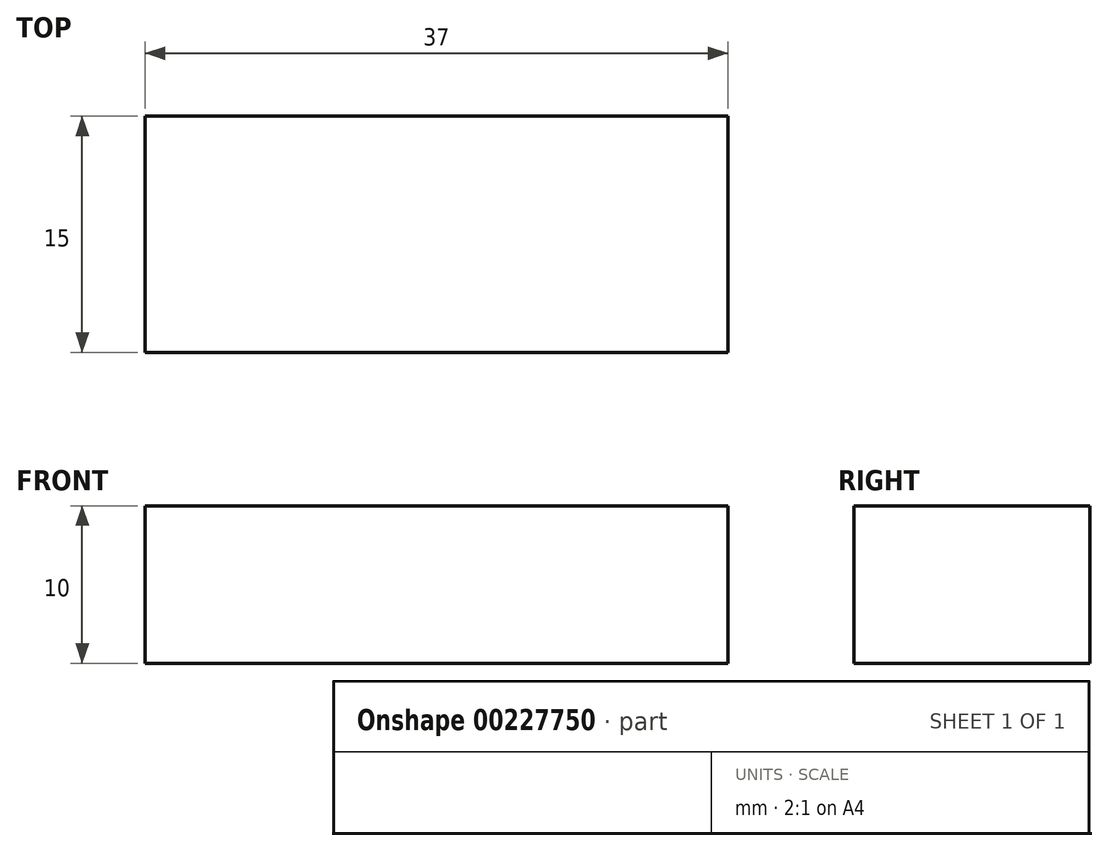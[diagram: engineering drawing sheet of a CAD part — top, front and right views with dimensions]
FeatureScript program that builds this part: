
annotation { "Feature Type Name" : "Feature", "Feature Type Description" : "" }
export const myFeature = defineFeature(function(context is Context, id is Id, definition is map)
    precondition{}
    {
        {
            var Q0;
            Q0=qCreatedBy(makeId("Top.planeOp"),FACE);
            var sketch = newSketch(context, id + "F0", { "sketchPlane" : qUnion([Q0])});
            skLineSegment(sketch, "E0.bottom", {"start": v(-18.5, 7.5) * mm, "end": v(18.5, 7.5) * mm});
            skLineSegment(sketch, "E0.top", {"start": v(-18.5, -7.5) * mm, "end": v(18.5, -7.5) * mm});
            skLineSegment(sketch, "E0.left", {"start": v(-18.5, 7.5) * mm, "end": v(-18.5, -7.5) * mm});
            skLineSegment(sketch, "E0.right", {"start": v(18.5, 7.5) * mm, "end": v(18.5, -7.5) * mm});
            skPoint(sketch, "E1", {"position": v(0, 0) * mm});
            skPoint(sketch, "E1.positionSnap0", {"position": v(18.5, 0) * mm});
            skPoint(sketch, "E1.positionSnap1", {"position": v(0, -7.5) * mm});
            skSolve(sketch);
        }
        {
            var Q0;
            Q0=makeQuery(id+"F0.imprint","IMPRINT",FACE,{"disambiguationData":[TD([[makeQuery(id+"F0.imprint","IMPRINT",EDGE,{"derivedFrom":sQuery(id+"F0.wireOp",EDGE,"E0.bottom")}),-1.0]])]});
            extrude(context, id + "F1", {"entities" : qUnion([Q0]), "depth" : 10 * mm, "offsetDistance" : 25 * mm});
        }
    });
